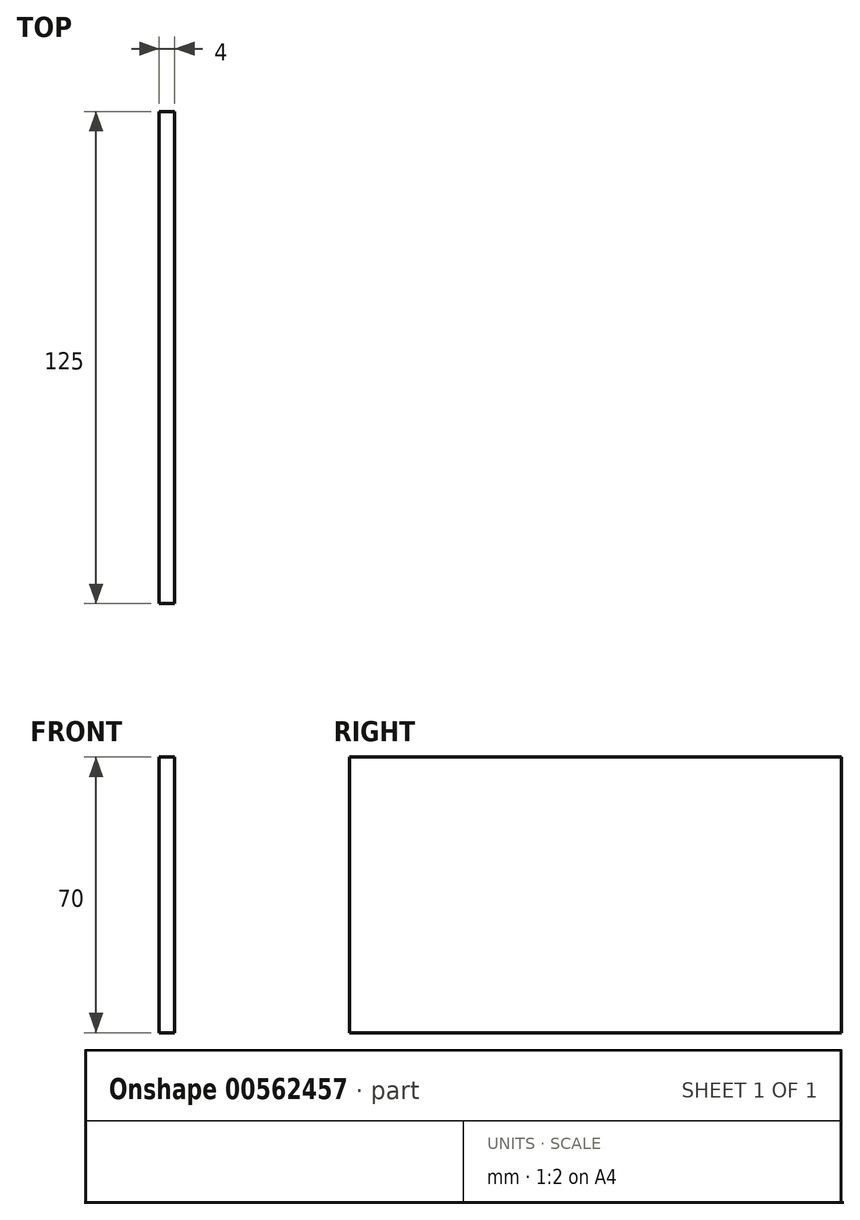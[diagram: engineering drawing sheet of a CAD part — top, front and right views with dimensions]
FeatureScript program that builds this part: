
annotation { "Feature Type Name" : "Feature", "Feature Type Description" : "" }
export const myFeature = defineFeature(function(context is Context, id is Id, definition is map)
    precondition{}
    {
        {
            var Q0;
            Q0=qCreatedBy(makeId("Right.planeOp"),FACE);
            var sketch = newSketch(context, id + "F0", { "sketchPlane" : qUnion([Q0])});
            skLineSegment(sketch, "E0.bottom", {"start": v(-62.5, 35) * mm, "end": v(62.5, 35) * mm});
            skLineSegment(sketch, "E0.top", {"start": v(-62.5, -35) * mm, "end": v(62.5, -35) * mm});
            skLineSegment(sketch, "E0.left", {"start": v(-62.5, 35) * mm, "end": v(-62.5, -35) * mm});
            skLineSegment(sketch, "E0.right", {"start": v(62.5, 35) * mm, "end": v(62.5, -35) * mm});
            skPoint(sketch, "E0.middle", {"position": v(0, 0) * mm});
            skSolve(sketch);
        }
        {
            var Q0;
            Q0=makeQuery(id+"F0.imprint","IMPRINT",FACE,{"disambiguationData":[TD([[makeQuery(id+"F0.imprint","IMPRINT",EDGE,{"derivedFrom":sQuery(id+"F0.wireOp",EDGE,"E0.bottom")}),-1.0]])]});
            extrude(context, id + "F1", {"entities" : qUnion([Q0]), "depth" : 4 * mm, "offsetDistance" : 25 * mm, "symmetric" : true});
        }
    });
